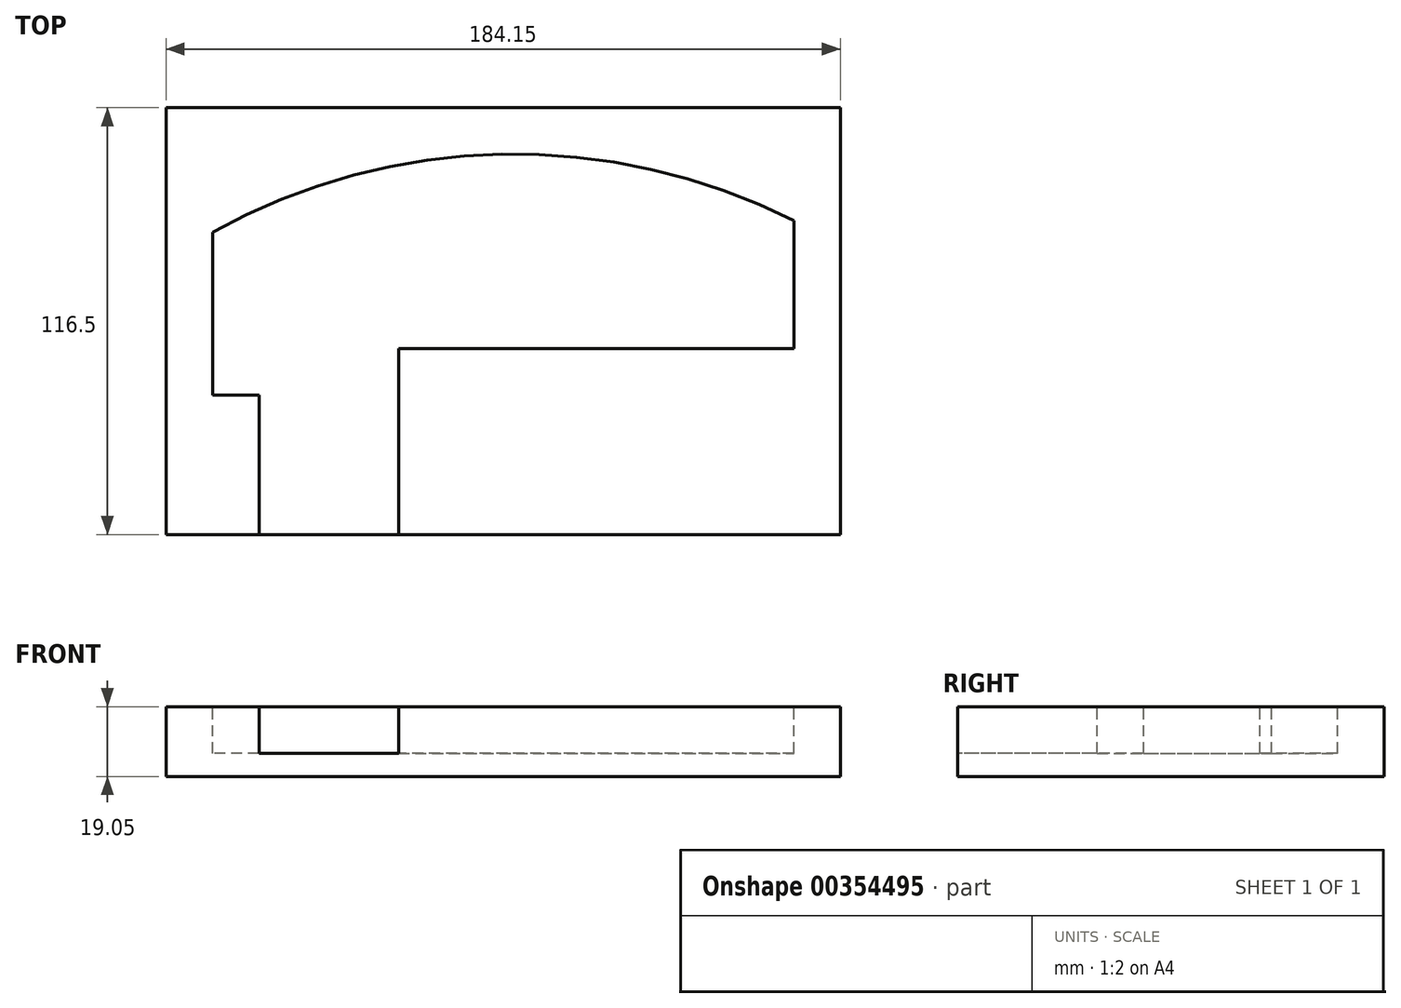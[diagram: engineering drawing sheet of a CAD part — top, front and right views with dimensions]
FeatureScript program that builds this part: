
annotation { "Feature Type Name" : "Feature", "Feature Type Description" : "" }
export const myFeature = defineFeature(function(context is Context, id is Id, definition is map)
    precondition{}
    {
        {
            var Q0;
            Q0=qCreatedBy(makeId("Top.planeOp"),FACE);
            var sketch = newSketch(context, id + "F0", { "sketchPlane" : qUnion([Q0])});
            skLineSegment(sketch, "E0.MirrorCS", {"start": v(111, 10.92) * mm, "end": v(98.3, 10.92) * mm});
            skLineSegment(sketch, "E1.MirrorCS", {"start": v(98.3, 10.92) * mm, "end": v(98.3, 55.37) * mm});
            skLineSegment(sketch, "E2.MirrorCS", {"start": v(149.1, 23.62) * mm, "end": v(257.04, 23.62) * mm});
            skLineSegment(sketch, "E3.MirrorCS", {"start": v(257.04, 23.62) * mm, "end": v(257.04, 58.55) * mm});
            skArc(sketch, "E4.MirrorCS", {"start": v(257.04, 58.55) * mm, "mid": v(177.28, 76.62) * mm, "end": v(98.3, 55.37) * mm});
            skLineSegment(sketch, "E5.MirrorCS", {"start": v(111, -14.48) * mm, "end": v(149.1, -14.48) * mm});
            skLineSegment(sketch, "E6.MirrorCS", {"start": v(111, 10.92) * mm, "end": v(111, -14.48) * mm});
            skLineSegment(sketch, "E7.MirrorCS", {"start": v(149.1, 23.62) * mm, "end": v(149.1, -14.48) * mm});
            skSolve(sketch);
        }
        {
            var Q0;
            Q0 = qSketchRegion(id + "F0", true);
            extrude(context, id + "F1", {"entities" : qUnion([Q0]), "depth" : 12.7 * mm});
        }
        {
            var Q0;
            Q0=makeQuery(id+"F1.opExtrude","CAP_FACE",FACE,{"disambiguationData":[OSD([sQuery(id+"F0.wireOp",EDGE,"E0.MirrorCS"),sQuery(id+"F0.wireOp",EDGE,"E1.MirrorCS"),sQuery(id+"F0.wireOp",EDGE,"E2.MirrorCS"),sQuery(id+"F0.wireOp",EDGE,"E3.MirrorCS"),sQuery(id+"F0.wireOp",EDGE,"E4.MirrorCS"),sQuery(id+"F0.wireOp",EDGE,"E5.MirrorCS"),sQuery(id+"F0.wireOp",EDGE,"E6.MirrorCS"),sQuery(id+"F0.wireOp",EDGE,"E7.MirrorCS")])],"isStart":true});
            var sketch = newSketch(context, id + "F2", { "sketchPlane" : qUnion([Q0])});
            skLineSegment(sketch, "E8.bottom", {"start": v(85.6, 27.18) * mm, "end": v(269.74, 27.18) * mm});
            skLineSegment(sketch, "E8.top", {"start": v(85.6, -89.32) * mm, "end": v(269.74, -89.32) * mm});
            skLineSegment(sketch, "E8.left", {"start": v(85.6, 27.18) * mm, "end": v(85.6, -89.32) * mm});
            skLineSegment(sketch, "E8.right", {"start": v(269.74, 27.18) * mm, "end": v(269.74, -89.32) * mm});
            skSolve(sketch);
        }
        {
            var Q0;
            Q0 = qSketchRegion(id + "F2", true);
            extrude(context, id + "F3", {"entities" : qUnion([Q0]), "operationType" : NewBodyOperationType.ADD, "depth" : 19.05 * mm});
        }
        {
            var Q0;
            Q0=makeQuery(id+"F1.opExtrude","CAP_FACE",FACE,{"disambiguationData":[OSD([sQuery(id+"F0.wireOp",EDGE,"E0.MirrorCS"),sQuery(id+"F0.wireOp",EDGE,"E1.MirrorCS"),sQuery(id+"F0.wireOp",EDGE,"E2.MirrorCS"),sQuery(id+"F0.wireOp",EDGE,"E3.MirrorCS"),sQuery(id+"F0.wireOp",EDGE,"E4.MirrorCS"),sQuery(id+"F0.wireOp",EDGE,"E5.MirrorCS"),sQuery(id+"F0.wireOp",EDGE,"E6.MirrorCS"),sQuery(id+"F0.wireOp",EDGE,"E7.MirrorCS")])],"isStart":false});
            extrude(context, id + "F4", {"entities" : qUnion([Q0]), "operationType" : NewBodyOperationType.REMOVE, "oppositeDirection" : true, "depth" : 25.4 * mm});
        }
        {
            var Q0;
            Q0=makeQuery(id+"F3.opExtrude","CAP_FACE",FACE,{"disambiguationData":[OSD([sQuery(id+"F2.wireOp",EDGE,"E8.bottom"),sQuery(id+"F2.wireOp",EDGE,"E8.top"),sQuery(id+"F2.wireOp",EDGE,"E8.left"),sQuery(id+"F2.wireOp",EDGE,"E8.right")])],"isStart":true});
            var sketch = newSketch(context, id + "F5", { "sketchPlane" : qUnion([Q0])});
            skLineSegment(sketch, "E9", {"start": v(111, -14.48) * mm, "end": v(111, -27.18) * mm});
            skLineSegment(sketch, "E10", {"start": v(111, -27.18) * mm, "end": v(149.1, -27.18) * mm});
            skLineSegment(sketch, "E11", {"start": v(149.1, -27.18) * mm, "end": v(149.1, -14.48) * mm});
            skLineSegment(sketch, "E12", {"start": v(149.1, -14.48) * mm, "end": v(111, -14.48) * mm});
            skSolve(sketch);
        }
        {
            var Q0;
            Q0=makeQuery(id+"F5.imprint","IMPRINT",FACE,{"disambiguationData":[TD([[makeQuery(id+"F5.imprint","IMPRINT",EDGE,{"derivedFrom":sQuery(id+"F5.wireOp",EDGE,"E9")}),1.0]])]});
            extrude(context, id + "F6", {"entities" : qUnion([Q0]), "operationType" : NewBodyOperationType.REMOVE, "oppositeDirection" : true, "depth" : 12.7 * mm});
        }
    });
